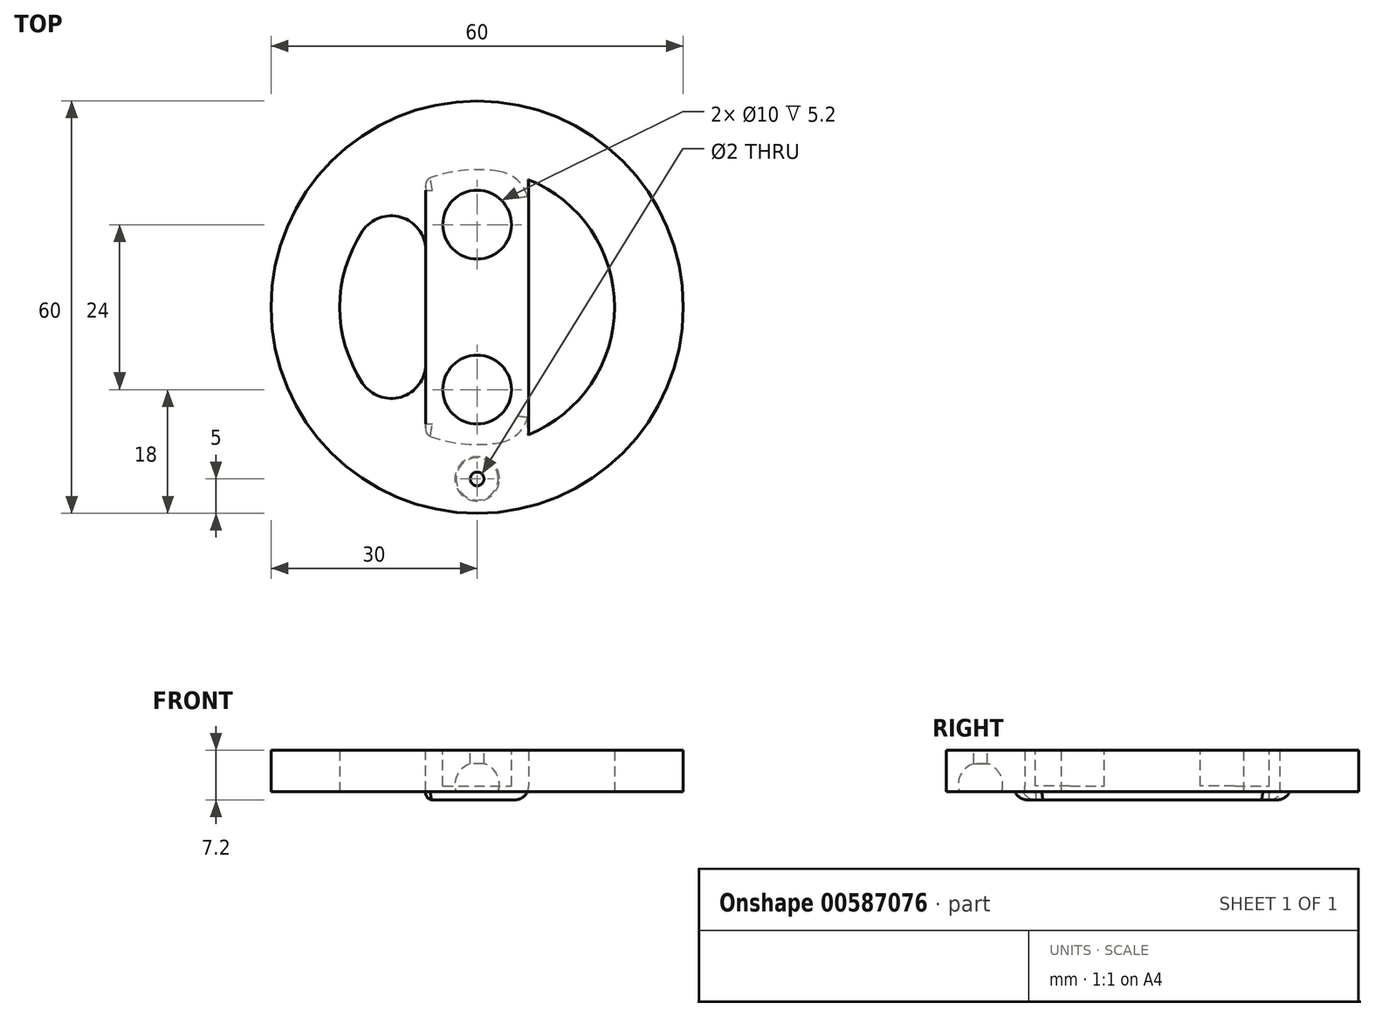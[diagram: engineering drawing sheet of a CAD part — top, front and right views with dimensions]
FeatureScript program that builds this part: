
annotation { "Feature Type Name" : "Feature", "Feature Type Description" : "" }
export const myFeature = defineFeature(function(context is Context, id is Id, definition is map)
    precondition{}
    {
        {
            var Q0;
            Q0=qCreatedBy(makeId("Top.planeOp"),FACE);
            var sketch = newSketch(context, id + "F0", { "sketchPlane" : qUnion([Q0])});
            skCircle(sketch, "E0", {"center": v(0, 0) * mm, "radius": 30 * mm});
            skCircle(sketch, "E1", {"center": v(0, 0) * mm, "radius": 20 * mm});
            skSolve(sketch);
        }
        {
            var Q0;
            Q0=makeQuery(id+"F0.imprint","IMPRINT",FACE,{"disambiguationData":[TD([[makeQuery(id+"F0.imprint","IMPRINT",EDGE,{"derivedFrom":sQuery(id+"F0.wireOp",EDGE,"E0")}),1.0]])]});
            extrude(context, id + "F1", {"entities" : qUnion([Q0]), "depth" : 6 * mm, "offsetDistance" : 25 * mm});
        }
        {
            var Q0;
            Q0=makeQuery(id+"F1.opExtrude","CAP_FACE",FACE,{"disambiguationData":[OSD([sQuery(id+"F0.wireOp",EDGE,"E0"),sQuery(id+"F0.wireOp",EDGE,"E1")])],"isStart":true});
            var sketch = newSketch(context, id + "F2", { "sketchPlane" : qUnion([Q0])});
            skCircle(sketch, "E2.0", {"center": v(0, 0) * mm, "radius": 30 * mm, "construction": true});
            skCircle(sketch, "E3.0", {"center": v(0, 0) * mm, "radius": 20 * mm, "construction": true});
            skLineSegment(sketch, "E4", {"start": v(0, 20) * mm, "end": v(0, 30) * mm, "construction": true});
            skPoint(sketch, "E5", {"position": v(0, 25) * mm});
            skSolve(sketch);
        }
        {
            var Q0;
            Q0=sQuery(id+"F2.wireOp",VERTEX,"E5");
            var Q1;
            Q1=qCreatedBy(makeId("Right.planeOp"),FACE);
            cPlane(context, id + "F3", {"entities" : qUnion([Q0, Q1]), "cplaneType" : CPlaneType.PLANE_POINT, "offset" : 25 * mm, "width" : 150 * mm, "height" : 150 * mm});
        }
        {
            var Q0;
            Q0=qCreatedBy(id+"F3.planeOp",FACE);
            var sketch = newSketch(context, id + "F4", { "sketchPlane" : qUnion([Q0])});
            skLineSegment(sketch, "E6.0", {"start": v(-30, 6) * mm, "end": v(30, 6) * mm, "construction": true});
            skLineSegment(sketch, "E7.0", {"start": v(-20, 0) * mm, "end": v(-30, 0) * mm, "construction": true});
            skLineSegment(sketch, "E8", {"start": v(-25, 0) * mm, "end": v(-25, 6) * mm, "construction": true});
            skArc(sketch, "E9", {"start": v(-26, 4.07) * mm, "mid": v(-28.2, 0.5) * mm, "end": v(-25, -2.23) * mm});
            skLineSegment(sketch, "E10", {"start": v(-25, 1) * mm, "end": v(-28.23, 1) * mm, "construction": true});
            skLineSegment(sketch, "E11", {"start": v(-25, -2.23) * mm, "end": v(-25, 4.23) * mm});
            skLineSegment(sketch, "E12", {"start": v(-26, 4.07) * mm, "end": v(-26, 6) * mm});
            skLineSegment(sketch, "E13", {"start": v(-26, 6) * mm, "end": v(-25, 6) * mm});
            skLineSegment(sketch, "E14", {"start": v(-25, 4.23) * mm, "end": v(-25, 6) * mm});
            skSolve(sketch);
        }
        {
            var Q0;
            Q0 = qSketchRegion(id + "F4", true);
            var Q1;
            Q1=sQuery(id+"F4.wireOp",EDGE,"E11");
            revolve(context, id + "F5", {"operationType" : NewBodyOperationType.REMOVE, "entities" : qUnion([Q0]), "axis" : qUnion([Q1]), "revolveType" : RevolveType.FULL, "oppositeDirection" : true});
        }
        {
            var Q0;
            Q0=makeQuery(id+"F1.opExtrude","CAP_FACE",FACE,{"disambiguationData":[OSD([sQuery(id+"F0.wireOp",EDGE,"E0"),sQuery(id+"F0.wireOp",EDGE,"E1")])],"isStart":true});
            var sketch = newSketch(context, id + "F6", { "sketchPlane" : qUnion([Q0])});
            skArc(sketch, "E15.0", {"start": v(7.5, 18.54) * mm, "mid": v(0, 20) * mm, "end": v(-7.5, 18.54) * mm});
            skLineSegment(sketch, "E16", {"start": v(0, 20) * mm, "end": v(0, -20) * mm, "construction": true});
            skLineSegment(sketch, "E17", {"start": v(-7.5, 18.54) * mm, "end": v(-7.5, -18.54) * mm});
            skLineSegment(sketch, "E18.MirrorCS", {"start": v(7.5, 18.54) * mm, "end": v(7.5, -18.54) * mm});
            skArc(sketch, "E19.trimOffspring", {"start": v(-7.5, -18.54) * mm, "mid": v(0, -20) * mm, "end": v(7.5, -18.54) * mm});
            skSolve(sketch);
        }
        {
            var Q0;
            Q0 = qSketchRegion(id + "F6", true);
            var Q1;
            Q1=makeQuery(id+"F1.opExtrude","CAP_FACE",FACE,{"disambiguationData":[OSD([sQuery(id+"F0.wireOp",EDGE,"E0"),sQuery(id+"F0.wireOp",EDGE,"E1")])],"isStart":false});
            extrude(context, id + "F7", {"entities" : qUnion([Q0]), "operationType" : NewBodyOperationType.ADD, "endBound" : BoundingType.UP_TO_SURFACE, "oppositeDirection" : true, "depth" : 25 * mm, "endBoundEntityFace" : qUnion([Q1]), "offsetDistance" : 25 * mm, "hasSecondDirection" : true, "secondDirectionOppositeDirection" : false, "secondDirectionDepth" : 1.2 * mm});
        }
        {
            var Q0;
            {var subQ0=sQuery(id+"F0.wireOp",EDGE,"E1");var subQ1=sQuery(id+"F6.wireOp",EDGE,"E18.MirrorCS");Q0=makeQuery(id+"F7.boolean.opBoolean","SPLIT",EDGE,{"disambiguationData":[topologyDisambiguationEdgeConnected([makeQuery(id+"F1.opExtrude","SWEPT_FACE",FACE,{"disambiguationData":[OSD([subQ0])]})])],"derivedFrom":makeQuery(id+"F7.opExtrude","SWEPT_EDGE",EDGE,{"disambiguationData":[OSD([subQ0,sQuery(id+"F6.wireOp",EDGE,"E15.0"),subQ1])]})});}
            var Q1;
            {var subQ0=sQuery(id+"F0.wireOp",EDGE,"E1");var subQ1=sQuery(id+"F6.wireOp",EDGE,"E17");Q1=makeQuery(id+"F7.boolean.opBoolean","SPLIT",EDGE,{"disambiguationData":[topologyDisambiguationEdgeConnected([makeQuery(id+"F1.opExtrude","SWEPT_FACE",FACE,{"disambiguationData":[OSD([subQ0])]})])],"derivedFrom":makeQuery(id+"F7.opExtrude","SWEPT_EDGE",EDGE,{"disambiguationData":[OSD([subQ0,sQuery(id+"F6.wireOp",EDGE,"E15.0"),subQ1])]})});}
            var Q2;
            {var subQ0=sQuery(id+"F0.wireOp",EDGE,"E1");var subQ1=sQuery(id+"F6.wireOp",EDGE,"E17");Q2=makeQuery(id+"F7.boolean.opBoolean","SPLIT",EDGE,{"disambiguationData":[topologyDisambiguationEdgeConnected([makeQuery(id+"F1.opExtrude","SWEPT_FACE",FACE,{"disambiguationData":[OSD([subQ0])]})])],"derivedFrom":makeQuery(id+"F7.opExtrude","SWEPT_EDGE",EDGE,{"disambiguationData":[OSD([subQ0,subQ1,sQuery(id+"F6.wireOp",EDGE,"E19.trimOffspring")])]})});}
            var Q3;
            {var subQ0=sQuery(id+"F0.wireOp",EDGE,"E1");var subQ1=sQuery(id+"F6.wireOp",EDGE,"E18.MirrorCS");Q3=makeQuery(id+"F7.boolean.opBoolean","SPLIT",EDGE,{"disambiguationData":[topologyDisambiguationEdgeConnected([makeQuery(id+"F1.opExtrude","SWEPT_FACE",FACE,{"disambiguationData":[OSD([subQ0])]})])],"derivedFrom":makeQuery(id+"F7.opExtrude","SWEPT_EDGE",EDGE,{"disambiguationData":[OSD([subQ0,subQ1,sQuery(id+"F6.wireOp",EDGE,"E19.trimOffspring")])]})});}
            fillet(context, id + "F8", {"entities" : qUnion([Q0, Q1, Q2, Q3]), "radius" : 5 * mm, "tangentPropagation" : true, "allowEdgeOverflow" : false});
        }
        {
            var Q0;
            Q0=makeQuery(id+"F7.opExtrude","CAP_EDGE",EDGE,{"disambiguationData":[OSD([sQuery(id+"F6.wireOp",EDGE,"E19.trimOffspring")])],"isStart":true});
            var Q1;
            Q1=makeQuery(id+"F7.opExtrude","CAP_EDGE",EDGE,{"disambiguationData":[OSD([sQuery(id+"F6.wireOp",EDGE,"E15.0")])],"isStart":true});
            fillet(context, id + "F9", {"entities" : qUnion([Q0, Q1]), "radius" : 2 * mm, "tangentPropagation" : true, "allowEdgeOverflow" : false});
        }
        {
            var Q0;
            Q0=makeQuery(id+"F7.opExtrude","CAP_EDGE",EDGE,{"disambiguationData":[OSD([sQuery(id+"F6.wireOp",EDGE,"E17")])],"isStart":true});
            var Q1;
            Q1=makeQuery(id+"F7.opExtrude","CAP_EDGE",EDGE,{"disambiguationData":[OSD([sQuery(id+"F6.wireOp",EDGE,"E18.MirrorCS")])],"isStart":true});
            fillet(context, id + "F10", {"entities" : qUnion([Q0, Q1]), "radius" : 1 * mm, "tangentPropagation" : true, "allowEdgeOverflow" : false});
        }
        {
            var Q0;
            {var subQ0=sQuery(id+"F0.wireOp",EDGE,"E1");var subQ1=sQuery(id+"F0.wireOp",EDGE,"E0");Q0=makeQuery(id+"F7.boolean.opBoolean","MERGE",FACE,{"derivedFrom":[makeQuery(id+"F1.opExtrude","CAP_FACE",FACE,{"disambiguationData":[OSD([subQ1,subQ0])],"isStart":false}),makeQuery(id+"F7.opExtrude","CAP_FACE",FACE,{"disambiguationData":[OSD([subQ1,subQ0])],"isStart":false})]});}
            var sketch = newSketch(context, id + "F11", { "sketchPlane" : qUnion([Q0])});
            skLineSegment(sketch, "E20.0", {"start": v(0, -20) * mm, "end": v(0, 20) * mm, "construction": true});
            skCircle(sketch, "E21", {"center": v(0, 12) * mm, "radius": 5 * mm});
            skLineSegment(sketch, "E22", {"start": v(-30, 0) * mm, "end": v(30, 0) * mm, "construction": true});
            skPoint(sketch, "E22.startSnap0", {"position": v(0, 0) * mm});
            skCircle(sketch, "E23.MirrorC", {"center": v(0, -12) * mm, "radius": 5 * mm});
            skSolve(sketch);
        }
        {
            var Q0;
            Q0 = qSketchRegion(id + "F11", true);
            var Q1;
            Q1=makeQuery(id+"F7.opExtrude","CAP_FACE",FACE,{"disambiguationData":[OSD([sQuery(id+"F6.wireOp",EDGE,"E15.0"),sQuery(id+"F6.wireOp",EDGE,"E17"),sQuery(id+"F6.wireOp",EDGE,"E18.MirrorCS"),sQuery(id+"F6.wireOp",EDGE,"E19.trimOffspring")])],"isStart":true});
            extrude(context, id + "F12", {"entities" : qUnion([Q0]), "operationType" : NewBodyOperationType.REMOVE, "endBound" : BoundingType.UP_TO_SURFACE, "oppositeDirection" : true, "depth" : 25 * mm, "endBoundEntityFace" : qUnion([Q1]), "hasOffset" : true, "offsetDistance" : 2 * mm});
        }
    });
